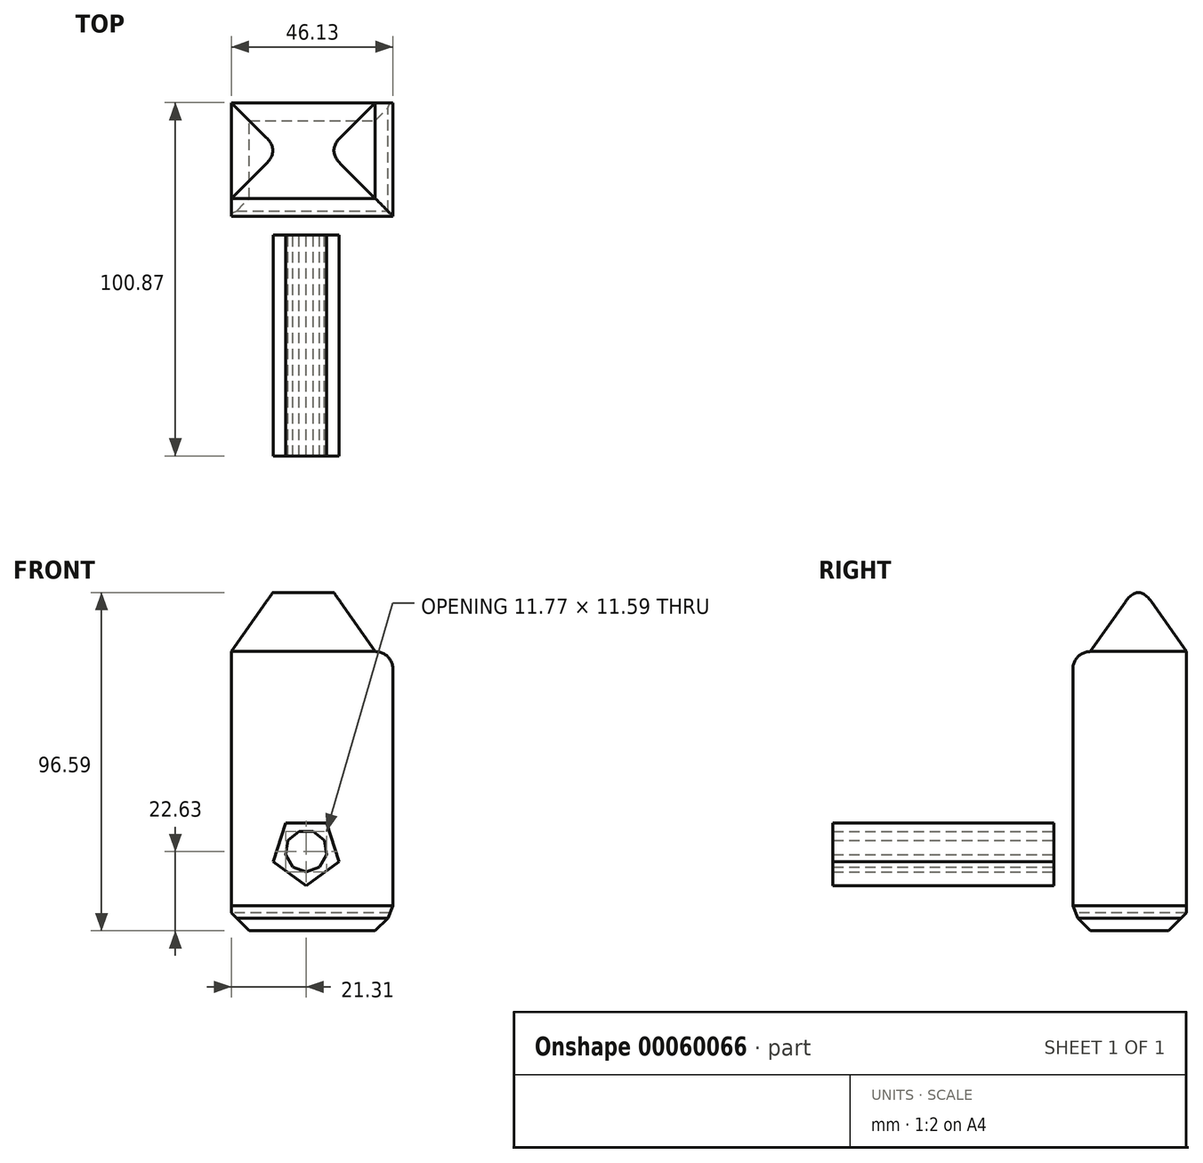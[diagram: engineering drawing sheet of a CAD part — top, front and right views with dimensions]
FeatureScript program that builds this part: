
annotation { "Feature Type Name" : "Feature", "Feature Type Description" : "" }
export const myFeature = defineFeature(function(context is Context, id is Id, definition is map)
    precondition{}
    {
        {
            var Q0;
            Q0=qCreatedBy(makeId("Top.planeOp"),FACE);
            var sketch = newSketch(context, id + "F0", { "sketchPlane" : qUnion([Q0])});
            skLineSegment(sketch, "E0.bottom", {"start": v(-21.31, 5.4) * mm, "end": v(24.82, 5.4) * mm});
            skLineSegment(sketch, "E0.top", {"start": v(-21.31, 37.8) * mm, "end": v(24.82, 37.8) * mm});
            skLineSegment(sketch, "E0.left", {"start": v(-21.31, 5.4) * mm, "end": v(-21.31, 37.8) * mm});
            skLineSegment(sketch, "E0.right", {"start": v(24.82, 5.4) * mm, "end": v(24.82, 37.8) * mm});
            skSolve(sketch);
        }
        {
            var Q0;
            Q0 = qSketchRegion(id + "F0", true);
            extrude(context, id + "F1", {"entities" : qUnion([Q0]), "depth" : 79.75 * mm});
        }
        {
            var Q0;
            Q0=makeQuery(id+"F1.opExtrude","CAP_EDGE",EDGE,{"disambiguationData":[OSD([sQuery(id+"F0.wireOp",EDGE,"E0.right")])],"isStart":false});
            var Q1;
            Q1=makeQuery(id+"F1.opExtrude","CAP_EDGE",EDGE,{"disambiguationData":[OSD([sQuery(id+"F0.wireOp",EDGE,"E0.bottom")])],"isStart":false});
            fillet(context, id + "F2", {"entities" : qUnion([Q0, Q1]), "radius" : 5.08 * mm, "tangentPropagation" : true, "allowEdgeOverflow" : false});
        }
        {
            var Q0;
            Q0=makeQuery(id+"F1.opExtrude","CAP_EDGE",EDGE,{"disambiguationData":[OSD([sQuery(id+"F0.wireOp",EDGE,"E0.bottom")])],"isStart":true});
            var Q1;
            Q1=makeQuery(id+"F1.opExtrude","CAP_EDGE",EDGE,{"disambiguationData":[OSD([sQuery(id+"F0.wireOp",EDGE,"E0.right")])],"isStart":true});
            var Q2;
            Q2=makeQuery(id+"F1.opExtrude","CAP_EDGE",EDGE,{"disambiguationData":[OSD([sQuery(id+"F0.wireOp",EDGE,"E0.left")])],"isStart":true});
            var Q3;
            Q3=makeQuery(id+"F1.opExtrude","CAP_EDGE",EDGE,{"disambiguationData":[OSD([sQuery(id+"F0.wireOp",EDGE,"E0.top")])],"isStart":true});
            chamfer(context, id + "F3", {"entities" : qUnion([Q0, Q1, Q2, Q3]), "width" : 5.08 * mm, "tangentPropagation" : true});
        }
        {
            var Q0;
            {var subQ0=sQuery(id+"F0.wireOp",EDGE,"E0.right");Q0=makeQuery(id+"F3.opChamfer","BLEND_EDGE",EDGE,{"blendedFrom":[makeQuery(id+"F1.opExtrude","CAP_EDGE",EDGE,{"disambiguationData":[OSD([subQ0])],"isStart":true}),makeQuery(id+"F1.opExtrude","SWEPT_FACE",FACE,{"disambiguationData":[OSD([subQ0])]})],"blendedInto":[makeQuery(id+"F1.opExtrude","SWEPT_FACE",FACE,{"disambiguationData":[OSD([subQ0])]})]});}
            var Q1;
            {var subQ0=sQuery(id+"F0.wireOp",EDGE,"E0.bottom");Q1=makeQuery(id+"F3.opChamfer","BLEND_EDGE",EDGE,{"blendedFrom":[makeQuery(id+"F1.opExtrude","CAP_EDGE",EDGE,{"disambiguationData":[OSD([subQ0])],"isStart":true}),makeQuery(id+"F1.opExtrude","SWEPT_FACE",FACE,{"disambiguationData":[OSD([subQ0])]})],"blendedInto":[makeQuery(id+"F1.opExtrude","SWEPT_FACE",FACE,{"disambiguationData":[OSD([subQ0])]})]});}
            chamfer(context, id + "F4", {"entities" : qUnion([Q0, Q1]), "width" : 5.08 * mm, "tangentPropagation" : true});
        }
        {
            var Q0;
            Q0=makeQuery(id+"F1.opExtrude","CAP_FACE",FACE,{"disambiguationData":[OSD([sQuery(id+"F0.wireOp",EDGE,"E0.bottom"),sQuery(id+"F0.wireOp",EDGE,"E0.top"),sQuery(id+"F0.wireOp",EDGE,"E0.left"),sQuery(id+"F0.wireOp",EDGE,"E0.right")])],"isStart":false});
            extrude(context, id + "F5", {"entities" : qUnion([Q0]), "operationType" : NewBodyOperationType.ADD, "endBound" : BoundingType.SYMMETRIC, "depth" : 41.36 * mm, "hasDraft" : true, "draftAngle" : 35 * degree, "draftPullDirection" : true});
        }
        {
            var Q0;
            {var subQ0=sQuery(id+"F0.wireOp",EDGE,"E0.top");var subQ1=sQuery(id+"F0.wireOp",EDGE,"E0.right");var subQ2=sQuery(id+"F0.wireOp",EDGE,"E0.left");var subQ3=sQuery(id+"F0.wireOp",EDGE,"E0.bottom");Q0=makeQuery(id+"F5.*.draftFirst.opDraft","TWEAK_EDGE",EDGE,{"derivedFrom":[makeQuery(id+"F5.*.split.splitOp","SPLIT",FACE,{"derivedFrom":makeQuery(id+"F5.opExtrude","SWEPT_FACE",FACE,{"disambiguationData":[OSD([subQ3,subQ0,subQ2,subQ1]),TDD([makeQuery(id+"F2.opFillet","BLEND_EDGE",EDGE,{"blendedFrom":[makeQuery(id+"F1.opExtrude","CAP_EDGE",EDGE,{"disambiguationData":[OSD([subQ3])],"isStart":false}),makeQuery(id+"F1.opExtrude","CAP_FACE",FACE,{"disambiguationData":[OSD([subQ3,subQ0,subQ2,subQ1])],"isStart":false})],"blendedInto":[makeQuery(id+"F1.opExtrude","CAP_FACE",FACE,{"disambiguationData":[OSD([subQ3,subQ0,subQ2,subQ1])],"isStart":false})]})])]})}),makeQuery(id+"F5.*.split.splitOp","SPLIT",FACE,{"derivedFrom":makeQuery(id+"F5.opExtrude","SWEPT_FACE",FACE,{"disambiguationData":[OSD([subQ0])]})})]});}
            fillet(context, id + "F6", {"entities" : qUnion([Q0]), "radius" : 4.57 * mm, "rho" : 0.5, "crossSection" : FilletCrossSection.CONIC, "allowEdgeOverflow" : false});
        }
        {
            var Q0;
            Q0=qCreatedBy(makeId("Front.planeOp"),FACE);
            var sketch = newSketch(context, id + "F7", { "sketchPlane" : qUnion([Q0])});
            skCircle(sketch, "E1.cCircle", {"center": v(0, 22.81) * mm, "radius": 7.99 * mm, "construction": true});
            skLineSegment(sketch, "E1.0", {"start": v(-5.8, 30.8) * mm, "end": v(5.8, 30.8) * mm});
            skLineSegment(sketch, "E1.1", {"start": v(5.8, 30.8) * mm, "end": v(9.4, 19.76) * mm});
            skLineSegment(sketch, "E1.2", {"start": v(9.4, 19.76) * mm, "end": v(0, 12.93) * mm});
            skLineSegment(sketch, "E1.3", {"start": v(0, 12.93) * mm, "end": v(-9.4, 19.76) * mm});
            skLineSegment(sketch, "E1.4", {"start": v(-9.4, 19.76) * mm, "end": v(-5.8, 30.8) * mm});
            skPoint(sketch, "E1.0.midPoint", {"position": v(0, 30.8) * mm});
            skCircle(sketch, "E2.cCircle", {"center": v(0, 22.81) * mm, "radius": 5.61 * mm, "construction": true});
            skLineSegment(sketch, "E2.0", {"start": v(-2.04, 28.42) * mm, "end": v(2.04, 28.42) * mm});
            skLineSegment(sketch, "E2.1", {"start": v(2.04, 28.42) * mm, "end": v(5.17, 25.8) * mm});
            skLineSegment(sketch, "E2.2", {"start": v(5.17, 25.8) * mm, "end": v(5.88, 21.77) * mm});
            skLineSegment(sketch, "E2.3", {"start": v(5.88, 21.77) * mm, "end": v(3.84, 18.23) * mm});
            skLineSegment(sketch, "E2.4", {"start": v(3.84, 18.23) * mm, "end": v(0, 16.84) * mm});
            skLineSegment(sketch, "E2.5", {"start": v(0, 16.84) * mm, "end": v(-3.84, 18.23) * mm});
            skLineSegment(sketch, "E2.6", {"start": v(-3.84, 18.23) * mm, "end": v(-5.88, 21.77) * mm});
            skLineSegment(sketch, "E2.7", {"start": v(-5.88, 21.77) * mm, "end": v(-5.17, 25.8) * mm});
            skLineSegment(sketch, "E2.8", {"start": v(-5.17, 25.8) * mm, "end": v(-2.04, 28.42) * mm});
            skPoint(sketch, "E2.0.midPoint", {"position": v(0, 28.42) * mm});
            skSolve(sketch);
        }
        {
            var Q0;
            Q0 = qSketchRegion(id + "F7", true);
            extrude(context, id + "F8", {"entities" : qUnion([Q0]), "depth" : 63.06 * mm});
        }
    });
